# Revit family: 272603e9-0872-4cef-8805-f811aafbdc41
name_source: partatom
category: Plumbing Fixtures
revit_build: Autodesk Revit 2016 (Build: 20161004_0715(x64)
units: mm (PartAtom-declared; Revit-internal decimal feet)

## family parameters
Cut with Voids When Loaded = No
Host = Face
OmniClass Number = 23.45.05.14.17
OmniClass Title = Showers
Part Type = Normal
Room Calculation Point = No
Round Connector Dimension = Use Diameter
Shared = Yes

## types (1)
- SH330
    Assembly Code = C1030210
    CW Connection = No
    Cap Location from Back = 0' - 1 11/16"
    Cover Height = 0' - 2 9/16"
    Cover Height Control = 0' - 2 9/16"
    Cut to Height = No
    Default Elevation = 4' - 0"
    Depth = 0' - 2 1/4"
    Description = Ligature Resistant Shower Head
    Finish = Aluminum-BSP-Chrome
    HW Connection = No
    HWFU = 0
    Height = 0' - 4"
    Inset Finish = Aluminum-BSP-Chrome
    Manufacturer = Behavioral Safety Products
    Model = SH330
    Product Documentation Link = http://besafeprod.com
    Product Page URL = http://besafeprod.com
    Product data url = https://bimobject.com
    Type Image = <None>
    URL = http://besafeprod.com
    Utility = No
    Vent Connection = No
    Waste Connection = No
    Water Flow = 0 GPM
    Water In Connection Description 1 = Hot Water Connection
    Width = 0' - 4"

## geometry (parser evidence)
native form markers: Blend x4, Sweep x1
no freeform markers — native parametric forms only
